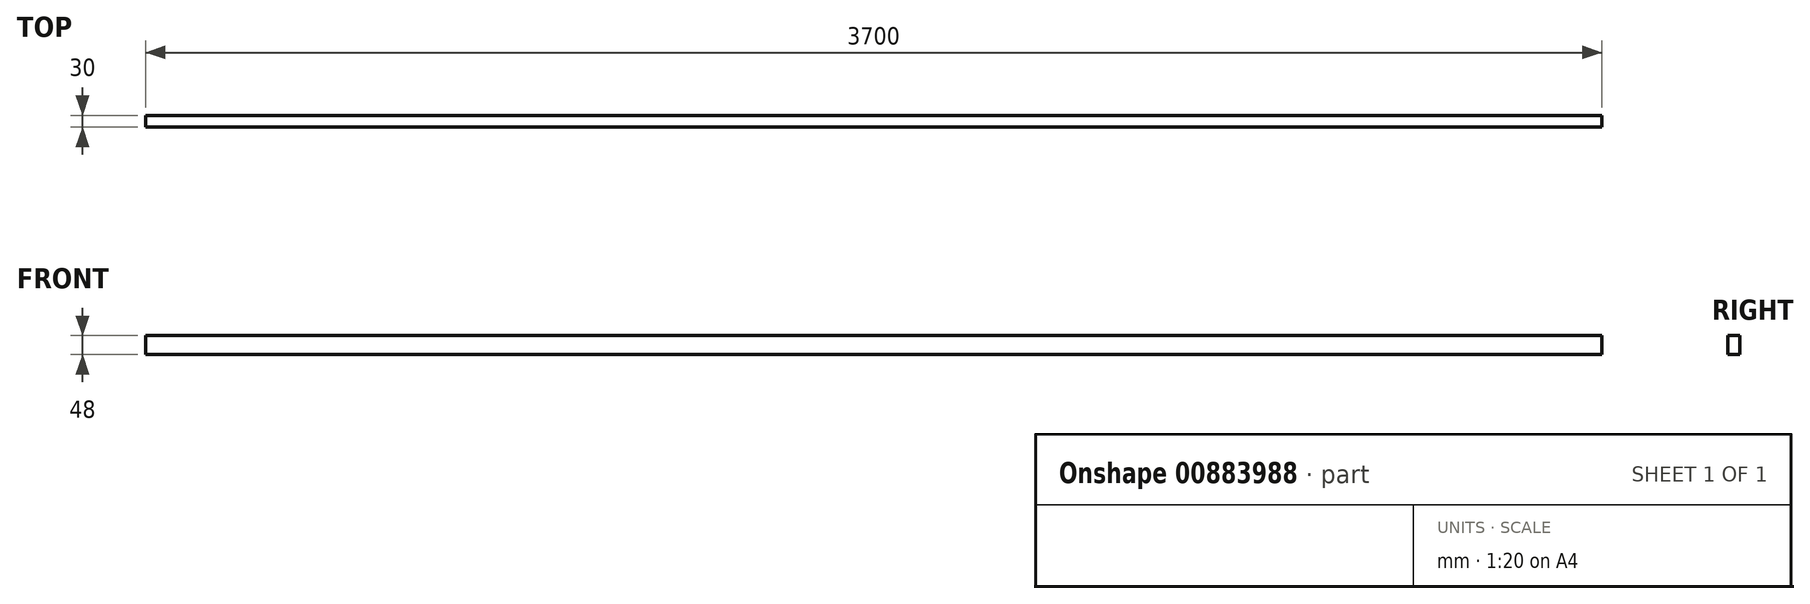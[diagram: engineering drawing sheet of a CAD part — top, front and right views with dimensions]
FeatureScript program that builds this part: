
annotation { "Feature Type Name" : "Feature", "Feature Type Description" : "" }
export const myFeature = defineFeature(function(context is Context, id is Id, definition is map)
    precondition{}
    {
        {
            var Q0;
            Q0=qCreatedBy(makeId("Top.planeOp"),FACE);
            var sketch = newSketch(context, id + "F0", { "sketchPlane" : qUnion([Q0])});
            skLineSegment(sketch, "E0.bottom", {"start": v(1850, -15) * mm, "end": v(-1850, -15) * mm});
            skLineSegment(sketch, "E0.top", {"start": v(1850, 15) * mm, "end": v(-1850, 15) * mm});
            skLineSegment(sketch, "E0.left", {"start": v(1850, -15) * mm, "end": v(1850, 15) * mm});
            skLineSegment(sketch, "E0.right", {"start": v(-1850, -15) * mm, "end": v(-1850, 15) * mm});
            skPoint(sketch, "E0.middle", {"position": v(0, 0) * mm});
            skSolve(sketch);
        }
        {
            var Q0;
            Q0=makeQuery(id+"F0.imprint","IMPRINT",FACE,{"disambiguationData":[TD([[makeQuery(id+"F0.imprint","IMPRINT",EDGE,{"derivedFrom":sQuery(id+"F0.wireOp",EDGE,"E0.bottom")}),-1.0]])]});
            extrude(context, id + "F1", {"entities" : qUnion([Q0]), "oppositeDirection" : true, "depth" : 48 * mm, "offsetDistance" : 25 * mm});
        }
    });
